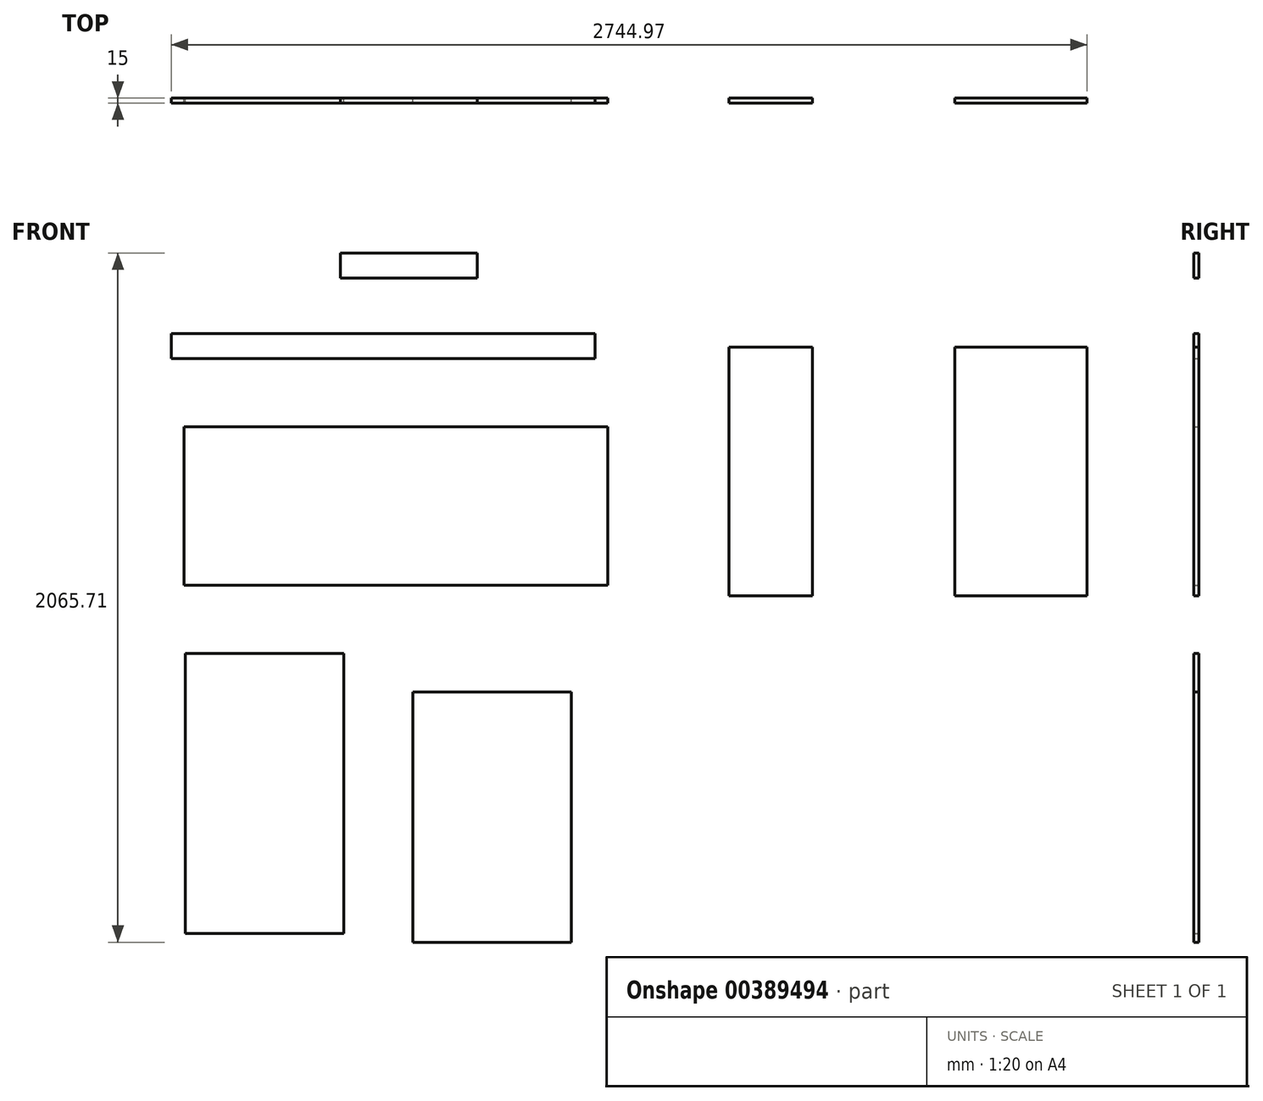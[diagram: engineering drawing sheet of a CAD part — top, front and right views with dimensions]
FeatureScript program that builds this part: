
annotation { "Feature Type Name" : "Feature", "Feature Type Description" : "" }
export const myFeature = defineFeature(function(context is Context, id is Id, definition is map)
    precondition{}
    {
        {
            var Q0;
            Q0=qCreatedBy(makeId("Front.planeOp"),FACE);
            var sketch = newSketch(context, id + "F0", { "sketchPlane" : qUnion([Q0])});
            skLineSegment(sketch, "E0.bottom", {"start": v(-1203.69, 66.22) * mm, "end": v(66.31, 66.22) * mm});
            skLineSegment(sketch, "E0.top", {"start": v(-1203.69, -8.78) * mm, "end": v(66.31, -8.78) * mm});
            skLineSegment(sketch, "E0.left", {"start": v(-1203.69, 66.22) * mm, "end": v(-1203.69, -8.78) * mm});
            skLineSegment(sketch, "E0.right", {"start": v(66.31, 66.22) * mm, "end": v(66.31, -8.78) * mm});
            skSolve(sketch);
        }
        {
            var Q0;
            Q0=makeQuery(id+"F0.imprint","IMPRINT",FACE,{"disambiguationData":[TD([[makeQuery(id+"F0.imprint","IMPRINT",EDGE,{"derivedFrom":sQuery(id+"F0.wireOp",EDGE,"E0.bottom")}),-1.0]])]});
            extrude(context, id + "F1", {"entities" : qUnion([Q0]), "depth" : 15 * mm, "offsetDistance" : 25 * mm});
        }
        {
            var Q0;
            Q0=qCreatedBy(makeId("Front.planeOp"),FACE);
            var sketch = newSketch(context, id + "F2", { "sketchPlane" : qUnion([Q0])});
            skLineSegment(sketch, "E1.bottom", {"start": v(-1166.23, -212.69) * mm, "end": v(103.77, -212.69) * mm});
            skLineSegment(sketch, "E1.top", {"start": v(-1166.23, -687.69) * mm, "end": v(103.77, -687.69) * mm});
            skLineSegment(sketch, "E1.left", {"start": v(-1166.23, -212.69) * mm, "end": v(-1166.23, -687.69) * mm});
            skLineSegment(sketch, "E1.right", {"start": v(103.77, -212.69) * mm, "end": v(103.77, -687.69) * mm});
            skSolve(sketch);
        }
        {
            var Q0;
            Q0=makeQuery(id+"F2.imprint","IMPRINT",FACE,{"disambiguationData":[TD([[makeQuery(id+"F2.imprint","IMPRINT",EDGE,{"derivedFrom":sQuery(id+"F2.wireOp",EDGE,"E1.bottom")}),-1.0]])]});
            extrude(context, id + "F3", {"entities" : qUnion([Q0]), "depth" : 15 * mm, "offsetDistance" : 25 * mm});
        }
        {
            var Q0;
            Q0=qCreatedBy(makeId("Front.planeOp"),FACE);
            var sketch = newSketch(context, id + "F4", { "sketchPlane" : qUnion([Q0])});
            skLineSegment(sketch, "E2.bottom", {"start": v(-1161.54, -892.1) * mm, "end": v(-686.54, -892.1) * mm});
            skLineSegment(sketch, "E2.top", {"start": v(-1161.54, -1732.1) * mm, "end": v(-686.54, -1732.1) * mm});
            skLineSegment(sketch, "E2.left", {"start": v(-1161.54, -892.1) * mm, "end": v(-1161.54, -1732.1) * mm});
            skLineSegment(sketch, "E2.right", {"start": v(-686.54, -892.1) * mm, "end": v(-686.54, -1732.1) * mm});
            skSolve(sketch);
        }
        {
            var Q0;
            Q0=makeQuery(id+"F4.imprint","IMPRINT",FACE,{"disambiguationData":[TD([[makeQuery(id+"F4.imprint","IMPRINT",EDGE,{"derivedFrom":sQuery(id+"F4.wireOp",EDGE,"E2.bottom")}),-1.0]])]});
            extrude(context, id + "F5", {"entities" : qUnion([Q0]), "depth" : 15 * mm, "offsetDistance" : 25 * mm});
        }
        {
            var Q0;
            Q0=qCreatedBy(makeId("Front.planeOp"),FACE);
            var sketch = newSketch(context, id + "F6", { "sketchPlane" : qUnion([Q0])});
            skLineSegment(sketch, "E3.bottom", {"start": v(-696.69, 307.92) * mm, "end": v(-286.69, 307.92) * mm});
            skLineSegment(sketch, "E3.top", {"start": v(-696.69, 232.92) * mm, "end": v(-286.69, 232.92) * mm});
            skLineSegment(sketch, "E3.left", {"start": v(-696.69, 307.92) * mm, "end": v(-696.69, 232.92) * mm});
            skLineSegment(sketch, "E3.right", {"start": v(-286.69, 307.92) * mm, "end": v(-286.69, 232.92) * mm});
            skSolve(sketch);
        }
        {
            var Q0;
            Q0=makeQuery(id+"F6.imprint","IMPRINT",FACE,{"disambiguationData":[TD([[makeQuery(id+"F6.imprint","IMPRINT",EDGE,{"derivedFrom":sQuery(id+"F6.wireOp",EDGE,"E3.bottom")}),-1.0]])]});
            extrude(context, id + "F7", {"entities" : qUnion([Q0]), "depth" : 15 * mm, "offsetDistance" : 25 * mm});
        }
        {
            var Q0;
            Q0=qCreatedBy(makeId("Front.planeOp"),FACE);
            var sketch = newSketch(context, id + "F8", { "sketchPlane" : qUnion([Q0])});
            skLineSegment(sketch, "E4.bottom", {"start": v(-480.11, -1007.79) * mm, "end": v(-5.11, -1007.79) * mm});
            skLineSegment(sketch, "E4.top", {"start": v(-480.11, -1757.79) * mm, "end": v(-5.11, -1757.79) * mm});
            skLineSegment(sketch, "E4.left", {"start": v(-480.11, -1007.79) * mm, "end": v(-480.11, -1757.79) * mm});
            skLineSegment(sketch, "E4.right", {"start": v(-5.11, -1007.79) * mm, "end": v(-5.11, -1757.79) * mm});
            skSolve(sketch);
        }
        {
            var Q0;
            Q0=makeQuery(id+"F8.imprint","IMPRINT",FACE,{"disambiguationData":[TD([[makeQuery(id+"F8.imprint","IMPRINT",EDGE,{"derivedFrom":sQuery(id+"F8.wireOp",EDGE,"E4.bottom")}),-1.0]])]});
            extrude(context, id + "F9", {"entities" : qUnion([Q0]), "depth" : 15 * mm, "offsetDistance" : 25 * mm});
        }
        {
            var Q0;
            Q0=qCreatedBy(makeId("Front.planeOp"),FACE);
            var sketch = newSketch(context, id + "F10", { "sketchPlane" : qUnion([Q0])});
            skLineSegment(sketch, "E5.bottom", {"start": v(1144.28, 25.48) * mm, "end": v(1541.28, 25.48) * mm});
            skLineSegment(sketch, "E5.top", {"start": v(1144.28, -719.52) * mm, "end": v(1541.28, -719.52) * mm});
            skLineSegment(sketch, "E5.left", {"start": v(1144.28, 25.48) * mm, "end": v(1144.28, -719.52) * mm});
            skLineSegment(sketch, "E5.right", {"start": v(1541.28, 25.48) * mm, "end": v(1541.28, -719.52) * mm});
            skLineSegment(sketch, "E6.bottom", {"start": v(468.11, 25.48) * mm, "end": v(718.11, 25.48) * mm});
            skLineSegment(sketch, "E6.top", {"start": v(468.11, -719.52) * mm, "end": v(718.11, -719.52) * mm});
            skLineSegment(sketch, "E6.left", {"start": v(468.11, 25.48) * mm, "end": v(468.11, -719.52) * mm});
            skLineSegment(sketch, "E6.right", {"start": v(718.11, 25.48) * mm, "end": v(718.11, -719.52) * mm});
            skSolve(sketch);
        }
        {
            var Q0;
            Q0=makeQuery(id+"F10.imprint","IMPRINT",FACE,{"disambiguationData":[TD([[makeQuery(id+"F10.imprint","IMPRINT",EDGE,{"derivedFrom":sQuery(id+"F10.wireOp",EDGE,"E5.bottom")}),-1.0]])]});
            extrude(context, id + "F11", {"entities" : qUnion([Q0]), "depth" : 15 * mm, "offsetDistance" : 25 * mm});
        }
        {
            var Q0;
            Q0=makeQuery(id+"F10.imprint","IMPRINT",FACE,{"disambiguationData":[TD([[makeQuery(id+"F10.imprint","IMPRINT",EDGE,{"derivedFrom":sQuery(id+"F10.wireOp",EDGE,"E6.bottom")}),-1.0]])]});
            extrude(context, id + "F12", {"entities" : qUnion([Q0]), "depth" : 15 * mm, "offsetDistance" : 25 * mm});
        }
    });
